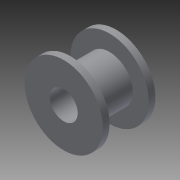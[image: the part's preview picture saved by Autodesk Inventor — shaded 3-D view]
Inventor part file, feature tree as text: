
AUTODESK INVENTOR PART (.ipt)
format: ipt  version: 2013 (Build 170138000, 138)  size: 94,208 bytes
history: native  units: mm
features: revolve x1, sketch x1
ambient origin geometry x8: Origin, YZ Plane, XZ Plane, XY Plane, X Axis, Y Axis, Z Axis, Center Point
bodies: Solid1 (feature_tree)
feature tree (2):
  revolve  "Revolution1"  [1 undecoded]
  sketch  "Sketch1"  dims[d0=2.5mm d2=9.4mm d3=1.2mm d4=1.2mm d5=7.0mm d6=4.15mm d7=90.0deg]
note: 1 required parameter value undecoded (feature->parameter linkage not recoverable at this tier; creation-order binding heuristic only, values carry confidence <= 0.55)
